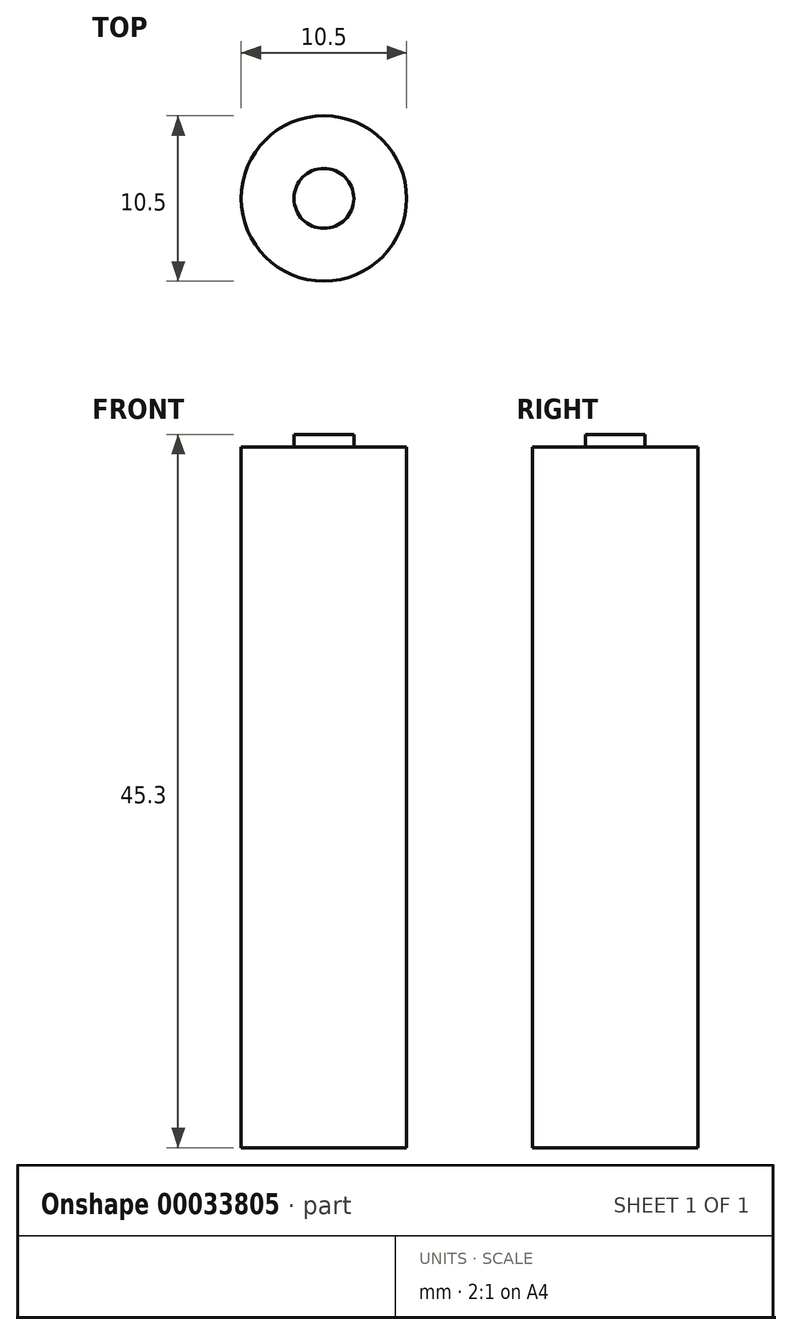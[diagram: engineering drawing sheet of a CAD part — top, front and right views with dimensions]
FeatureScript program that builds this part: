
annotation { "Feature Type Name" : "Feature", "Feature Type Description" : "" }
export const myFeature = defineFeature(function(context is Context, id is Id, definition is map)
    precondition{}
    {
        {
            var Q0;
            Q0=qCreatedBy(makeId("Top.planeOp"),FACE);
            var sketch = newSketch(context, id + "F0", { "sketchPlane" : qUnion([Q0])});
            skCircle(sketch, "E0", {"center": v(0, 0) * mm, "radius": 5.25 * mm});
            skSolve(sketch);
        }
        {
            var Q0;
            Q0=makeQuery(id+"F0.imprint","IMPRINT",FACE,{"disambiguationData":[TD([[makeQuery(id+"F0.imprint","IMPRINT",EDGE,{"derivedFrom":sQuery(id+"F0.wireOp",EDGE,"E0")}),1.0]])]});
            extrude(context, id + "F1", {"entities" : qUnion([Q0]), "depth" : 44.5 * mm});
        }
        {
            var Q0;
            Q0=makeQuery(id+"F1.opExtrude","CAP_FACE",FACE,{"disambiguationData":[OSD([sQuery(id+"F0.wireOp",EDGE,"E0")])],"isStart":false});
            var sketch = newSketch(context, id + "F2", { "sketchPlane" : qUnion([Q0])});
            skCircle(sketch, "E1", {"center": v(0, 0) * mm, "radius": 1.9 * mm});
            skSolve(sketch);
        }
        {
            var Q0;
            Q0=makeQuery(id+"F2.imprint","IMPRINT",FACE,{"disambiguationData":[TD([[makeQuery(id+"F2.imprint","IMPRINT",EDGE,{"derivedFrom":sQuery(id+"F2.wireOp",EDGE,"E1")}),1.0]])]});
            extrude(context, id + "F3", {"entities" : qUnion([Q0]), "operationType" : NewBodyOperationType.ADD, "depth" : .8 * mm});
        }
    });
